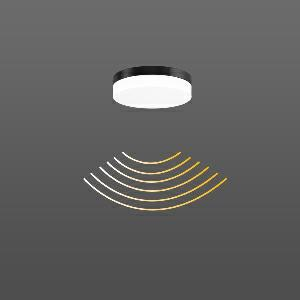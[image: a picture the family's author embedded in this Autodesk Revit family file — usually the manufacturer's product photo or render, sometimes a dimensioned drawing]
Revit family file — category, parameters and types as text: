
# Revit family: flat_slim_round_312132_0031_19_52d9
name_source: partatom
category: Lighting Fixtures
units: mm (PartAtom-declared; Revit-internal decimal feet)

## family parameters
Cut with Voids When Loaded = No
Host = Face
Light Source = No
Part Type = Normal
Room Calculation Point = No
Round Connector Dimension = Use Diameter
Shared = No

## types (1)
- FLAT SLIM round (1 x LED Modul 830, 1000 lm, 3000)
    Apparent Load = 12 VA
    CIE Flux Codes = 42 72 91 89 100
    Color Rendering = 80
    Color Temperature = 3000
    Default Elevation = 1800 mm
    Height = 63 mm
    Lamp = 1 x LED Modul 830
    Lamp Light Flux = 1000 lm
    Lamp count = 1
    Length = 230 mm
    Lifetime = 50000 h
    Luminous efficacy = 83 lm/W
    Manufacturer = RZB
    ModVariant = No
    Model = 312132.0031.19
    Mounting Place = Ceiling, Wall
    Mounting Type = Surface mounted
    Number of Poles = 1
    OnlyDefault = Yes
    Power Factor = 1
    Product Name = FLAT SLIM round
    Product group = Surface mounted ceiling and wall luminaires
    ProductGroupID = 305
    Protection Class = Protection class I
    Protection Degree = IP 65
    RLX_Detail_Level = 1
    RLX_Emergency_Light_Flux = 0 lm
    RLX_Emergency_Type = 0
    RLX_Emergency_Type_DB = No
    RlxData = <blob elided: 31985 chars, md5=161e58f7>
    Socket = socket
    Standby Power = 0 W
    System Light Flux = 1000 lm
    System Power = 12 W
    Type Comments = Product without accessories
    Type Image = 312132.0031.19.jpg
    URL = http://relux.com
    VarID = ---
    Voltage = 230 V
    Voltage Range = 220-240 V
    Weight = 0.00 kg
    Width = 0 mm  [stored 0 ft]

note: [stored X ft] marks values corroborated as IEEE doubles in the binary element streams (Revit-internal decimal feet)

## geometry (parser evidence)
native form markers: Blend x4, Sweep x11
no freeform markers — native parametric forms only
